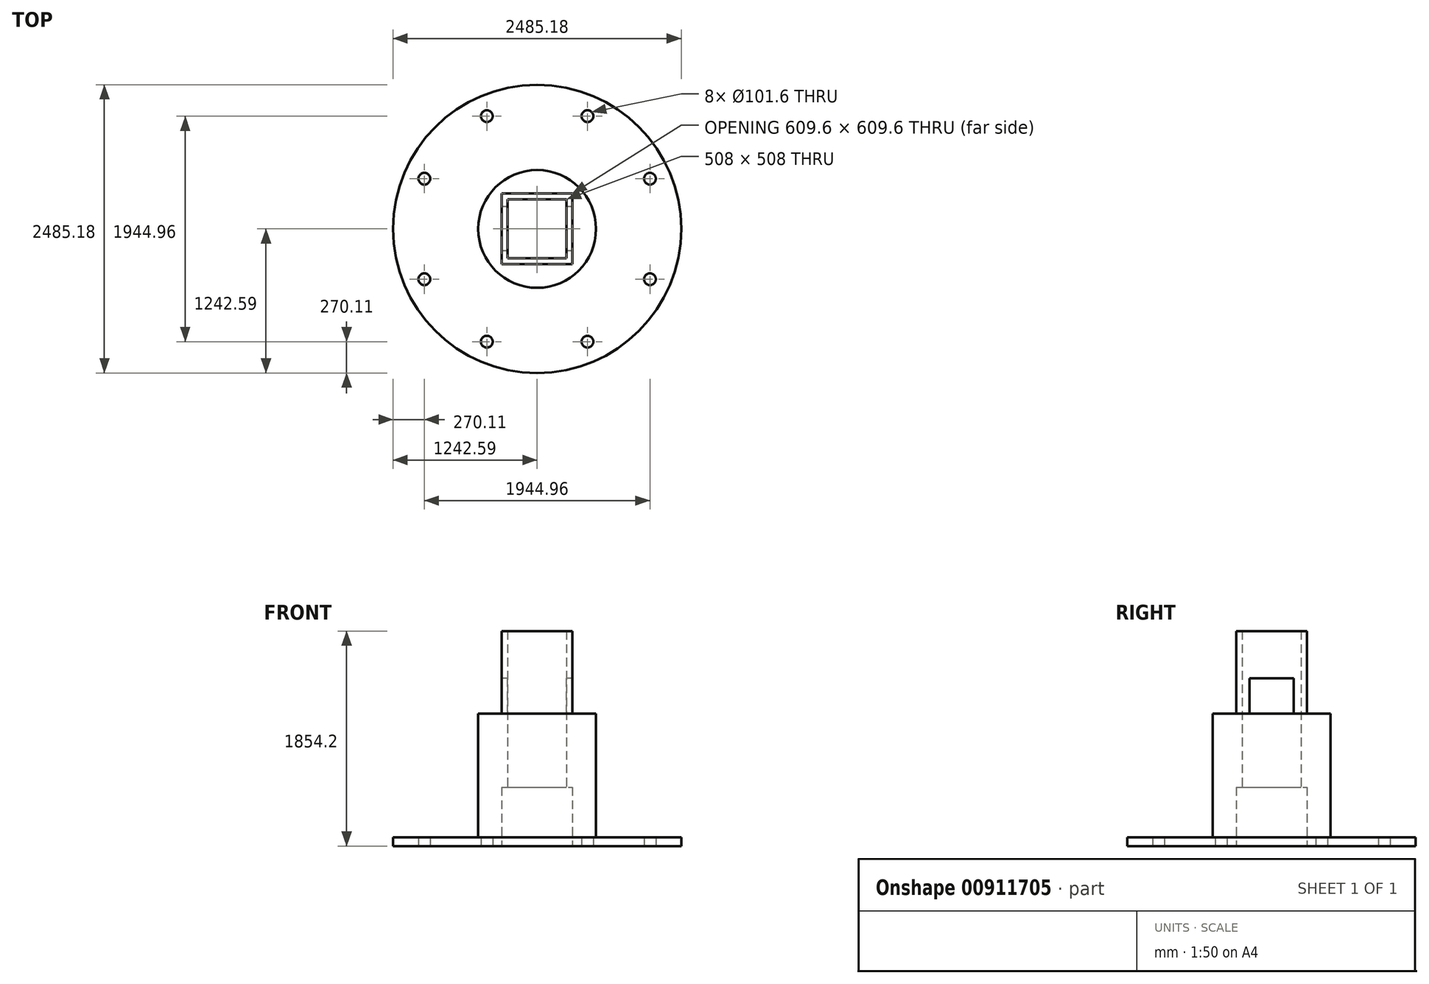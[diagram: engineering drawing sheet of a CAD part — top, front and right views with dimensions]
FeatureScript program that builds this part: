
annotation { "Feature Type Name" : "Feature", "Feature Type Description" : "" }
export const myFeature = defineFeature(function(context is Context, id is Id, definition is map)
    precondition{}
    {
        {
            var Q0;
            Q0=qCreatedBy(makeId("Top.planeOp"),FACE);
            var sketch = newSketch(context, id + "F0", { "sketchPlane" : qUnion([Q0])});
            skLineSegment(sketch, "E0.bottom", {"start": v(-330.2, -330.2) * mm, "end": v(330.2, -330.2) * mm});
            skLineSegment(sketch, "E0.top", {"start": v(-330.2, 330.2) * mm, "end": v(330.2, 330.2) * mm});
            skLineSegment(sketch, "E0.left", {"start": v(-330.2, -330.2) * mm, "end": v(-330.2, 330.2) * mm});
            skLineSegment(sketch, "E0.right", {"start": v(330.2, -330.2) * mm, "end": v(330.2, 330.2) * mm});
            skPoint(sketch, "E0.middle", {"position": v(0, 0) * mm});
            skCircle(sketch, "E1", {"center": v(0, 0) * mm, "radius": 1242.6 * mm});
            skLineSegment(sketch, "E2.bottom", {"start": v(-254, -254) * mm, "end": v(254, -254) * mm});
            skLineSegment(sketch, "E2.top", {"start": v(-254, 254) * mm, "end": v(254, 254) * mm});
            skLineSegment(sketch, "E2.left", {"start": v(-254, -254) * mm, "end": v(-254, 254) * mm});
            skLineSegment(sketch, "E2.right", {"start": v(254, -254) * mm, "end": v(254, 254) * mm});
            skLineSegment(sketch, "E3.bottom", {"start": v(-304.8, -304.8) * mm, "end": v(304.8, -304.8) * mm});
            skLineSegment(sketch, "E3.top", {"start": v(-304.8, 304.8) * mm, "end": v(304.8, 304.8) * mm});
            skLineSegment(sketch, "E3.left", {"start": v(-304.8, -304.8) * mm, "end": v(-304.8, 304.8) * mm});
            skLineSegment(sketch, "E3.right", {"start": v(304.8, -304.8) * mm, "end": v(304.8, 304.8) * mm});
            skCircle(sketch, "E4", {"center": v(0, 0) * mm, "radius": 508 * mm});
            skLineSegment(sketch, "E5", {"start": v(0, 0) * mm, "end": v(1454.17, -1454.17) * mm, "construction": true});
            skPoint(sketch, "E6", {"position": v(703.07, -703.07) * mm});
            skLineSegment(sketch, "E7", {"start": v(-1092.98, -2499.12) * mm, "end": v(2499.12, 1092.98) * mm, "construction": true});
            skCircle(sketch, "E8", {"center": v(433.66, -972.48) * mm, "radius": 50.8 * mm});
            skCircle(sketch, "E9", {"center": v(972.48, -433.66) * mm, "radius": 50.8 * mm});
            skCircle(sketch, "E10", {"center": v(1933.93, 1505.92) * mm, "radius": 50.8 * mm});
            skCircle(sketch, "E11", {"center": v(1933.93, 1505.92) * mm, "radius": 323.34 * mm});
            skLineSegment(sketch, "E12.1.0", {"start": v(2499.12, -1092.98) * mm, "end": v(-1092.98, 2499.12) * mm, "construction": true});
            skCircle(sketch, "E12.1.1", {"center": v(433.66, 972.48) * mm, "radius": 50.8 * mm});
            skCircle(sketch, "E12.1.2", {"center": v(972.48, 433.66) * mm, "radius": 50.8 * mm});
            skLineSegment(sketch, "E12.2.0", {"start": v(1092.98, 2499.12) * mm, "end": v(-2499.12, -1092.98) * mm, "construction": true});
            skCircle(sketch, "E12.2.1", {"center": v(-972.48, 433.66) * mm, "radius": 50.8 * mm});
            skCircle(sketch, "E12.2.2", {"center": v(-433.66, 972.48) * mm, "radius": 50.8 * mm});
            skLineSegment(sketch, "E12.3.0", {"start": v(-2499.12, 1092.98) * mm, "end": v(1092.98, -2499.12) * mm, "construction": true});
            skCircle(sketch, "E12.3.1", {"center": v(-433.66, -972.48) * mm, "radius": 50.8 * mm});
            skCircle(sketch, "E12.3.2", {"center": v(-972.48, -433.66) * mm, "radius": 50.8 * mm});
            skSolve(sketch);
        }
        {
            var Q0;
            Q0=makeQuery(id+"F0.imprint","IMPRINT",FACE,{"disambiguationData":[TD([[makeQuery(id+"F0.imprint","IMPRINT",EDGE,{"derivedFrom":sQuery(id+"F0.wireOp",EDGE,"E1")}),1.0]])]});
            extrude(context, id + "F1", {"entities" : qUnion([Q0]), "depth" : 76.2 * mm, "offsetDistance" : 25.4 * mm});
        }
        {
            var Q0;
            Q0=makeQuery(id+"F0.imprint","IMPRINT",FACE,{"disambiguationData":[TD([[makeQuery(id+"F0.imprint","IMPRINT",EDGE,{"derivedFrom":sQuery(id+"F0.wireOp",EDGE,"E0.bottom")}),-1.0]])]});
            var Q1;
            Q1=makeQuery(id+"F0.imprint","IMPRINT",FACE,{"disambiguationData":[TD([[makeQuery(id+"F0.imprint","IMPRINT",EDGE,{"derivedFrom":sQuery(id+"F0.wireOp",EDGE,"E0.bottom")}),1.0]])]});
            var Q2;
            Q2=makeQuery(id+"F0.imprint","IMPRINT",FACE,{"disambiguationData":[TD([[makeQuery(id+"F0.imprint","IMPRINT",EDGE,{"derivedFrom":sQuery(id+"F0.wireOp",EDGE,"E2.bottom")}),-1.0]])]});
            var Q3;
            Q3=makeQuery(id+"F0.imprint","IMPRINT",FACE,{"disambiguationData":[TD([[makeQuery(id+"F0.imprint","IMPRINT",EDGE,{"derivedFrom":sQuery(id+"F0.wireOp",EDGE,"E2.bottom")}),1.0]])]});
            extrude(context, id + "F2", {"entities" : qUnion([Q0, Q1, Q2, Q3]), "operationType" : NewBodyOperationType.ADD, "depth" : 1143 * mm, "offsetDistance" : 25.4 * mm});
        }
        {
            var Q0;
            Q0=makeQuery(id+"F0.imprint","IMPRINT",FACE,{"disambiguationData":[TD([[makeQuery(id+"F0.imprint","IMPRINT",EDGE,{"derivedFrom":sQuery(id+"F0.wireOp",EDGE,"E2.bottom")}),-1.0]])]});
            extrude(context, id + "F3", {"entities" : qUnion([Q0]), "operationType" : NewBodyOperationType.ADD, "depth" : 1854.2 * mm, "offsetDistance" : 25.4 * mm});
        }
        {
            var Q0;
            Q0=makeQuery(id+"F0.imprint","IMPRINT",FACE,{"disambiguationData":[TD([[makeQuery(id+"F0.imprint","IMPRINT",EDGE,{"derivedFrom":sQuery(id+"F0.wireOp",EDGE,"E2.bottom")}),1.0]])]});
            extrude(context, id + "F4", {"entities" : qUnion([Q0]), "operationType" : NewBodyOperationType.REMOVE, "depth" : 2540 * mm, "offsetDistance" : 25.4 * mm});
        }
        {
            var Q0;
            Q0=makeQuery(id+"F0.imprint","IMPRINT",FACE,{"disambiguationData":[TD([[makeQuery(id+"F0.imprint","IMPRINT",EDGE,{"derivedFrom":sQuery(id+"F0.wireOp",EDGE,"E2.bottom")}),-1.0]])]});
            extrude(context, id + "F5", {"entities" : qUnion([Q0]), "operationType" : NewBodyOperationType.REMOVE, "depth" : 508 * mm, "offsetDistance" : 25.4 * mm});
        }
        {
            var Q0;
            Q0=makeQuery(id+"F3.opExtrude","SWEPT_FACE",FACE,{"disambiguationData":[OSD([sQuery(id+"F0.wireOp",EDGE,"E3.left")])]});
            var sketch = newSketch(context, id + "F6", { "sketchPlane" : qUnion([Q0])});
            skLineSegment(sketch, "E13.bottom", {"start": v(-190.5, 1143) * mm, "end": v(190.5, 1143) * mm});
            skLineSegment(sketch, "E13.top", {"start": v(-190.5, 1447.8) * mm, "end": v(190.5, 1447.8) * mm});
            skLineSegment(sketch, "E13.left", {"start": v(-190.5, 1143) * mm, "end": v(-190.5, 1447.8) * mm});
            skLineSegment(sketch, "E13.right", {"start": v(190.5, 1143) * mm, "end": v(190.5, 1447.8) * mm});
            skSolve(sketch);
        }
        {
            var Q0;
            Q0=makeQuery(id+"F6.imprint","IMPRINT",FACE,{"disambiguationData":[TD([[makeQuery(id+"F6.imprint","IMPRINT",EDGE,{"derivedFrom":sQuery(id+"F6.wireOp",EDGE,"E13.bottom")}),1.0]])]});
            extrude(context, id + "F7", {"entities" : qUnion([Q0]), "operationType" : NewBodyOperationType.REMOVE, "oppositeDirection" : true, "depth" : 962.66 * mm, "offsetDistance" : 25.4 * mm});
        }
    });
